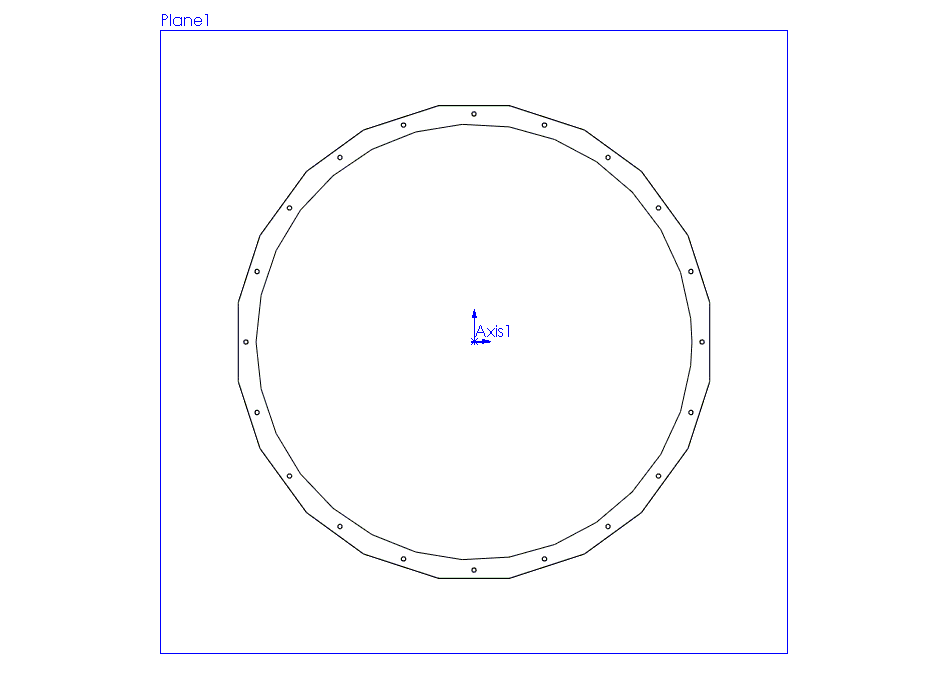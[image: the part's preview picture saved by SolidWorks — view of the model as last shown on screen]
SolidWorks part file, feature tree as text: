
SOLIDWORKS PART (.sldprt)
format: sldprt  version: not decoded by parser v0  size: 410,624 bytes
history: native  units: mm
features: sketch x3, cut_extrude x2, pattern_circular x2, material x1, extrude x1, plane x1, fillet x1 (+13 scaffold rows collapsed)
feature tree (24):
  scaffold x13  (default folders/planes/origin — collapsed)
  material  "Plain Carbon Steel"
  sketch  "Sketch1"  dims[D1=751.84mm D2=685.8mm]
  extrude  "Extrude1"  Depth=3.175mm
  plane  "Plane1"
  sketch  "Sketch2"  dims[c1.D1=717.55mm c1.D3=7.112mm c1.D2=361.95mm c2.D2=0.0deg c2.D3=19.05mm]
  cut_extrude  "Cut-Extrude1"  [1 undecoded]
  pattern_circular  "CirPattern1"  Count=20 Angle=360deg
  sketch  "Sketch3"  dims[D1=304.8mm]
  cut_extrude  "Cut-Extrude3"  [1 undecoded]
  pattern_circular  "CirPattern2"  Count=10 Angle=360deg
  fillet  "Fillet1"  Radius=9.525mm
decode coverage: 7 of 9 modeling features carry decoded parameters
note: 2 parameter values undecoded
note: suppression state not decoded; provenance and decode notes live in map.json
